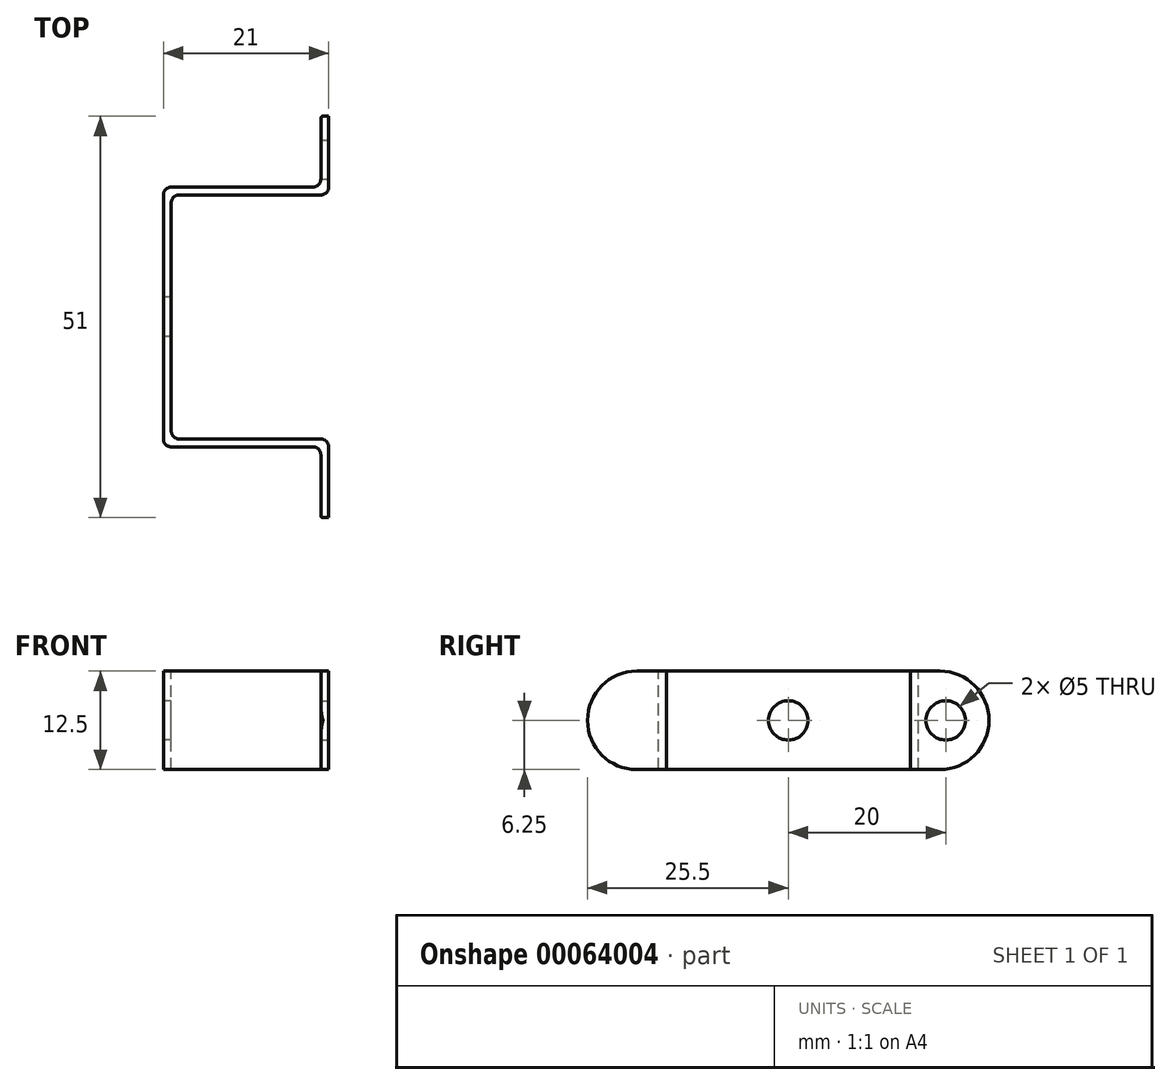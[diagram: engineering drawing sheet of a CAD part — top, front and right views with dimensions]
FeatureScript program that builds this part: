
annotation { "Feature Type Name" : "Feature", "Feature Type Description" : "" }
export const myFeature = defineFeature(function(context is Context, id is Id, definition is map)
    precondition{}
    {
        {
            var Q0;
            Q0=qCreatedBy(makeId("Top.planeOp"),FACE);
            var sketch = newSketch(context, id + "F0", { "sketchPlane" : qUnion([Q0])});
            skLineSegment(sketch, "E0", {"start": v(0, 34.86) * mm, "end": v(0, -34.86) * mm, "construction": true});
            skPoint(sketch, "E1", {"position": v(0, 0) * mm});
            skLineSegment(sketch, "E2", {"start": v(-28.43, 0) * mm, "end": v(28.43, 0) * mm, "construction": true});
            skLineSegment(sketch, "E3", {"start": v(0, 25.5) * mm, "end": v(0, 16.5) * mm});
            skLineSegment(sketch, "E4", {"start": v(-1, 15.5) * mm, "end": v(-19, 15.5) * mm});
            skLineSegment(sketch, "E5", {"start": v(-20, 14.5) * mm, "end": v(-20, 0) * mm});
            skPoint(sketch, "E6", {"position": v(0, 20) * mm});
            skLineSegment(sketch, "E7.0", {"start": v(-21, 15.5) * mm, "end": v(-21, 0) * mm});
            skLineSegment(sketch, "E7.1", {"start": v(-2, 16.5) * mm, "end": v(-20, 16.5) * mm});
            skLineSegment(sketch, "E7.2", {"start": v(-1, 25.22) * mm, "end": v(-1, 17.5) * mm});
            skLineSegment(sketch, "E8", {"start": v(-0.72, 25.5) * mm, "end": v(0, 25.5) * mm});
            skLineSegment(sketch, "E9", {"start": v(-21, 0) * mm, "end": v(-20, 0) * mm});
            skPoint(sketch, "E10.visualSharp", {"position": v(-1, 25.5) * mm});
            skArc(sketch, "E10.filletArc", {"start": v(-0.72, 25.5) * mm, "mid": v(-0.92, 25.42) * mm, "end": v(-1, 25.22) * mm});
            skPoint(sketch, "E11.visualSharp", {"position": v(-1, 16.5) * mm});
            skArc(sketch, "E11.filletArc", {"start": v(-2, 16.5) * mm, "mid": v(-1.3, 16.8) * mm, "end": v(-1, 17.5) * mm});
            skPoint(sketch, "E12.visualSharp", {"position": v(0, 15.5) * mm});
            skArc(sketch, "E12.filletArc", {"start": v(-1, 15.5) * mm, "mid": v(-0.3, 15.8) * mm, "end": v(0, 16.5) * mm});
            skPoint(sketch, "E13.visualSharp", {"position": v(-20, 15.5) * mm});
            skArc(sketch, "E13.filletArc", {"start": v(-19, 15.5) * mm, "mid": v(-19.7, 15.2) * mm, "end": v(-20, 14.5) * mm});
            skPoint(sketch, "E14.visualSharp", {"position": v(-21, 16.5) * mm});
            skArc(sketch, "E14.filletArc", {"start": v(-20, 16.5) * mm, "mid": v(-20.7, 16.2) * mm, "end": v(-21, 15.5) * mm});
            skLineSegment(sketch, "E15.MirrorCS", {"start": v(0, -25.5) * mm, "end": v(0, -16.5) * mm});
            skLineSegment(sketch, "E16.MirrorCS", {"start": v(-1, -25.22) * mm, "end": v(-1, -17.5) * mm});
            skPoint(sketch, "E17.MirrorP", {"position": v(-1, -25.5) * mm});
            skArc(sketch, "E18.MirrorCS", {"start": v(-0.72, -25.5) * mm, "mid": v(-0.92, -25.42) * mm, "end": v(-1, -25.22) * mm});
            skLineSegment(sketch, "E19.MirrorCS", {"start": v(-0.72, -25.5) * mm, "end": v(0, -25.5) * mm});
            skArc(sketch, "E20.MirrorCS", {"start": v(-2, -16.5) * mm, "mid": v(-1.3, -16.8) * mm, "end": v(-1, -17.5) * mm});
            skArc(sketch, "E21.MirrorCS", {"start": v(-1, -15.5) * mm, "mid": v(-0.3, -15.8) * mm, "end": v(0, -16.5) * mm});
            skLineSegment(sketch, "E22.MirrorCS", {"start": v(-2, -16.5) * mm, "end": v(-20, -16.5) * mm});
            skLineSegment(sketch, "E23.MirrorCS", {"start": v(-1, -15.5) * mm, "end": v(-19, -15.5) * mm});
            skArc(sketch, "E24.MirrorCS", {"start": v(-19, -15.5) * mm, "mid": v(-19.7, -15.2) * mm, "end": v(-20, -14.5) * mm});
            skArc(sketch, "E25.MirrorCS", {"start": v(-20, -16.5) * mm, "mid": v(-20.7, -16.2) * mm, "end": v(-21, -15.5) * mm});
            skLineSegment(sketch, "E26.MirrorCS", {"start": v(-21, -15.5) * mm, "end": v(-21, 0) * mm});
            skLineSegment(sketch, "E27.MirrorCS", {"start": v(-20, -14.5) * mm, "end": v(-20, 0) * mm});
            skSolve(sketch);
        }
        {
            var Q0;
            Q0=makeQuery(id+"F0.imprint","IMPRINT",FACE,{"disambiguationData":[TD([[makeQuery(id+"F0.imprint","IMPRINT",EDGE,{"derivedFrom":sQuery(id+"F0.wireOp",EDGE,"E9")}),-1.0]])]});
            var Q1;
            Q1=makeQuery(id+"F0.imprint","IMPRINT",FACE,{"disambiguationData":[TD([[makeQuery(id+"F0.imprint","IMPRINT",EDGE,{"derivedFrom":sQuery(id+"F0.wireOp",EDGE,"E3")}),-1.0]])]});
            extrude(context, id + "F1", {"entities" : qUnion([Q0, Q1]), "endBound" : BoundingType.SYMMETRIC, "oppositeDirection" : true, "depth" : 12.5 * mm});
        }
        {
            var Q0;
            Q0=makeQuery(id+"F1.opExtrude","SWEPT_FACE",FACE,{"disambiguationData":[OSD([sQuery(id+"F0.wireOp",EDGE,"E3")])]});
            var sketch = newSketch(context, id + "F2", { "sketchPlane" : qUnion([Q0])});
            skLineSegment(sketch, "E28", {"start": v(0, 17.39) * mm, "end": v(0, -17.39) * mm, "construction": true});
            skPoint(sketch, "E29", {"position": v(0, 0) * mm});
            skLineSegment(sketch, "E30", {"start": v(33.94, 0) * mm, "end": v(-33.94, 0) * mm, "construction": true});
            skCircle(sketch, "E31", {"center": v(20, 0) * mm, "radius": 2.5 * mm});
            skPoint(sketch, "E32", {"position": v(25.5, 0) * mm});
            skPoint(sketch, "E33.second.point", {"position": v(19.25, 6.25) * mm});
            skPoint(sketch, "E33.third.point", {"position": v(14.42, -3.97) * mm});
            skLineSegment(sketch, "E34", {"start": v(19.25, 6.25) * mm, "end": v(25.5, 6.25) * mm});
            skLineSegment(sketch, "E35", {"start": v(25.5, 6.25) * mm, "end": v(25.5, 0) * mm});
            skLineSegment(sketch, "E36", {"start": v(25.5, -6.25) * mm, "end": v(19.25, -6.25) * mm});
            skArc(sketch, "E37.trimOffspring", {"start": v(19.25, -6.25) * mm, "mid": v(25.5, 0) * mm, "end": v(19.25, 6.25) * mm});
            skCircle(sketch, "E38.MirrorC", {"center": v(-20, 0) * mm, "radius": 2.5 * mm});
            skArc(sketch, "E39.MirrorCS", {"start": v(-19.25, -6.25) * mm, "mid": v(-25.5, 0) * mm, "end": v(-19.25, 6.25) * mm});
            skLineSegment(sketch, "E40.MirrorCS", {"start": v(-25.5, -6.25) * mm, "end": v(-19.25, -6.25) * mm});
            skLineSegment(sketch, "E41.MirrorCS", {"start": v(-25.5, 6.25) * mm, "end": v(-25.5, 0) * mm});
            skLineSegment(sketch, "E42.MirrorCS", {"start": v(-19.25, 6.25) * mm, "end": v(-25.5, 6.25) * mm});
            skLineSegment(sketch, "E43", {"start": v(25.5, 0) * mm, "end": v(25.5, -6.25) * mm});
            skLineSegment(sketch, "E44", {"start": v(-25.5, 0) * mm, "end": v(-25.5, -6.25) * mm});
            skSolve(sketch);
        }
        {
            var Q0;
            {var subQ0=sQuery(id+"F2.wireOp",EDGE,"E34");Q0=makeQuery(id+"F2.imprint","IMPRINT",FACE,{"disambiguationData":[TD([[makeQuery(id+"F2.imprint","IMPRINT",EDGE,{"derivedFrom":subQ0}),1.0]])]});}
            var Q1;
            Q1=makeQuery(id+"F2.imprint","IMPRINT",FACE,{"disambiguationData":[TD([[makeQuery(id+"F2.imprint","IMPRINT",EDGE,{"derivedFrom":sQuery(id+"F2.wireOp",EDGE,"E31")}),1.0]])]});
            var Q2;
            {var subQ0=sQuery(id+"F2.wireOp",EDGE,"E36");Q2=makeQuery(id+"F2.imprint","IMPRINT",FACE,{"disambiguationData":[TD([[makeQuery(id+"F2.imprint","IMPRINT",EDGE,{"derivedFrom":subQ0}),-1.0]])]});}
            var Q3;
            Q3=makeQuery(id+"F2.imprint","IMPRINT",FACE,{"disambiguationData":[TD([[makeQuery(id+"F2.imprint","IMPRINT",EDGE,{"derivedFrom":sQuery(id+"F2.wireOp",EDGE,"E38.MirrorC")}),-1.0]])]});
            var Q4;
            {var subQ2=sQuery(id+"F2.wireOp",EDGE,"E41.MirrorCS");Q4=makeQuery(id+"F2.imprint","IMPRINT",FACE,{"disambiguationData":[TD([[makeQuery(id+"F2.imprint","IMPRINT",EDGE,{"derivedFrom":subQ2}),1.0]])]});}
            var Q5;
            {var subQ0=sQuery(id+"F2.wireOp",EDGE,"E40.MirrorCS");Q5=makeQuery(id+"F2.imprint","IMPRINT",FACE,{"disambiguationData":[TD([[makeQuery(id+"F2.imprint","IMPRINT",EDGE,{"derivedFrom":subQ0}),1.0]])]});}
            extrude(context, id + "F3", {"entities" : qUnion([Q0, Q1, Q2, Q3, Q4, Q5]), "operationType" : NewBodyOperationType.REMOVE, "endBound" : BoundingType.UP_TO_NEXT, "oppositeDirection" : true, "depth" : 25 * mm});
        }
        {
            var Q0;
            Q0=makeQuery(id+"F1.opExtrude","SWEPT_FACE",FACE,{"disambiguationData":[OSD([sQuery(id+"F0.wireOp",EDGE,"E7.0"),sQuery(id+"F0.wireOp",EDGE,"E26.MirrorCS")])]});
            var sketch = newSketch(context, id + "F4", { "sketchPlane" : qUnion([Q0])});
            skLineSegment(sketch, "E45", {"start": v(0, 10.62) * mm, "end": v(0, -10.62) * mm, "construction": true});
            skPoint(sketch, "E46", {"position": v(0, 0) * mm});
            skCircle(sketch, "E47", {"center": v(0, 0) * mm, "radius": 2.5 * mm});
            skSolve(sketch);
        }
        {
            var Q0;
            Q0 = qSketchRegion(id + "F4", true);
            extrude(context, id + "F5", {"entities" : qUnion([Q0]), "operationType" : NewBodyOperationType.REMOVE, "endBound" : BoundingType.UP_TO_NEXT, "oppositeDirection" : true, "depth" : 25 * mm});
        }
    });
